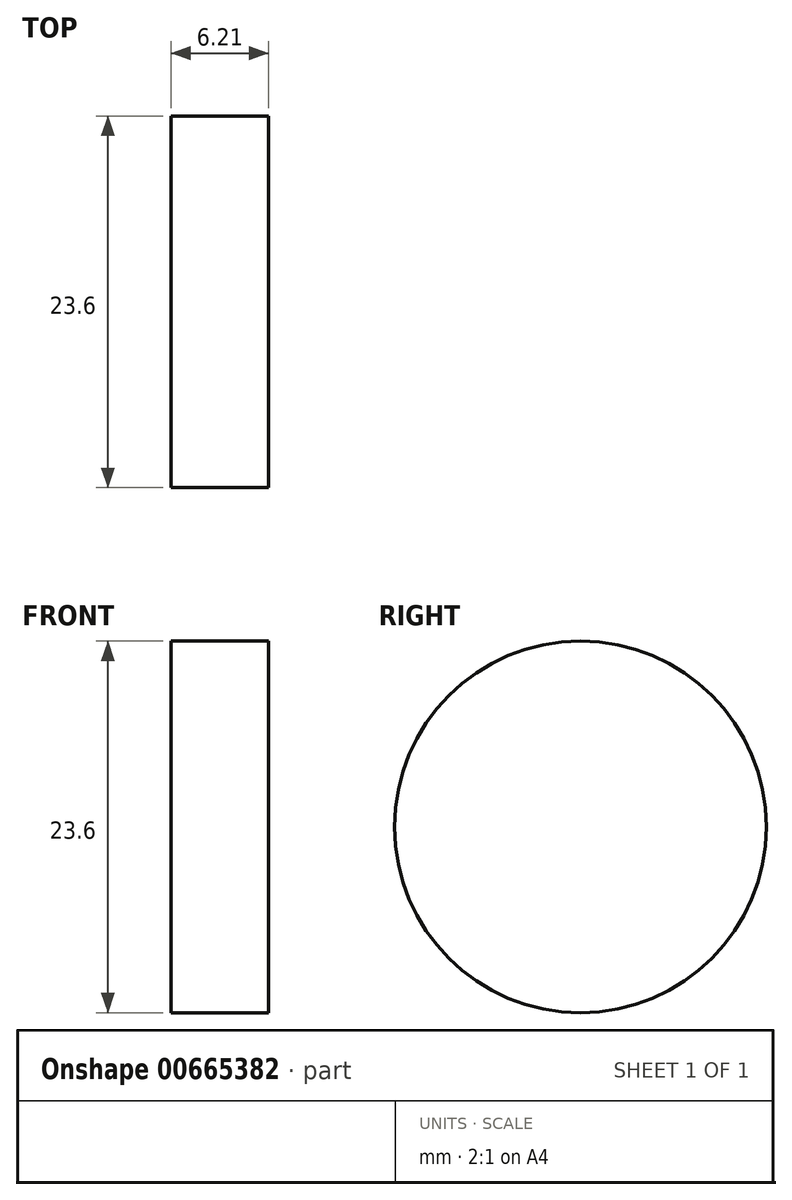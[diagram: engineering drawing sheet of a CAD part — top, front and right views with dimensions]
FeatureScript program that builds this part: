
annotation { "Feature Type Name" : "Feature", "Feature Type Description" : "" }
export const myFeature = defineFeature(function(context is Context, id is Id, definition is map)
    precondition{}
    {
        {
            var Q0;
            Q0=qCreatedBy(makeId("Right.planeOp"),FACE);
            var sketch = newSketch(context, id + "F0", { "sketchPlane" : qUnion([Q0])});
            skCircle(sketch, "E0", {"center": v(0, 0) * mm, "radius": 43.52 * mm});
            skCircle(sketch, "E1", {"center": v(0, 0) * mm, "radius": 11.8 * mm});
            skSolve(sketch);
        }
        {
            var Q0;
            Q0=makeQuery(id+"F0.imprint","IMPRINT",FACE,{"disambiguationData":[TD([[makeQuery(id+"F0.imprint","IMPRINT",EDGE,{"derivedFrom":sQuery(id+"F0.wireOp",EDGE,"E1")}),1.0]])]});
            extrude(context, id + "F1", {"entities" : qUnion([Q0]), "depth" : 6.2 * mm, "offsetDistance" : 25.4 * mm});
        }
    });
